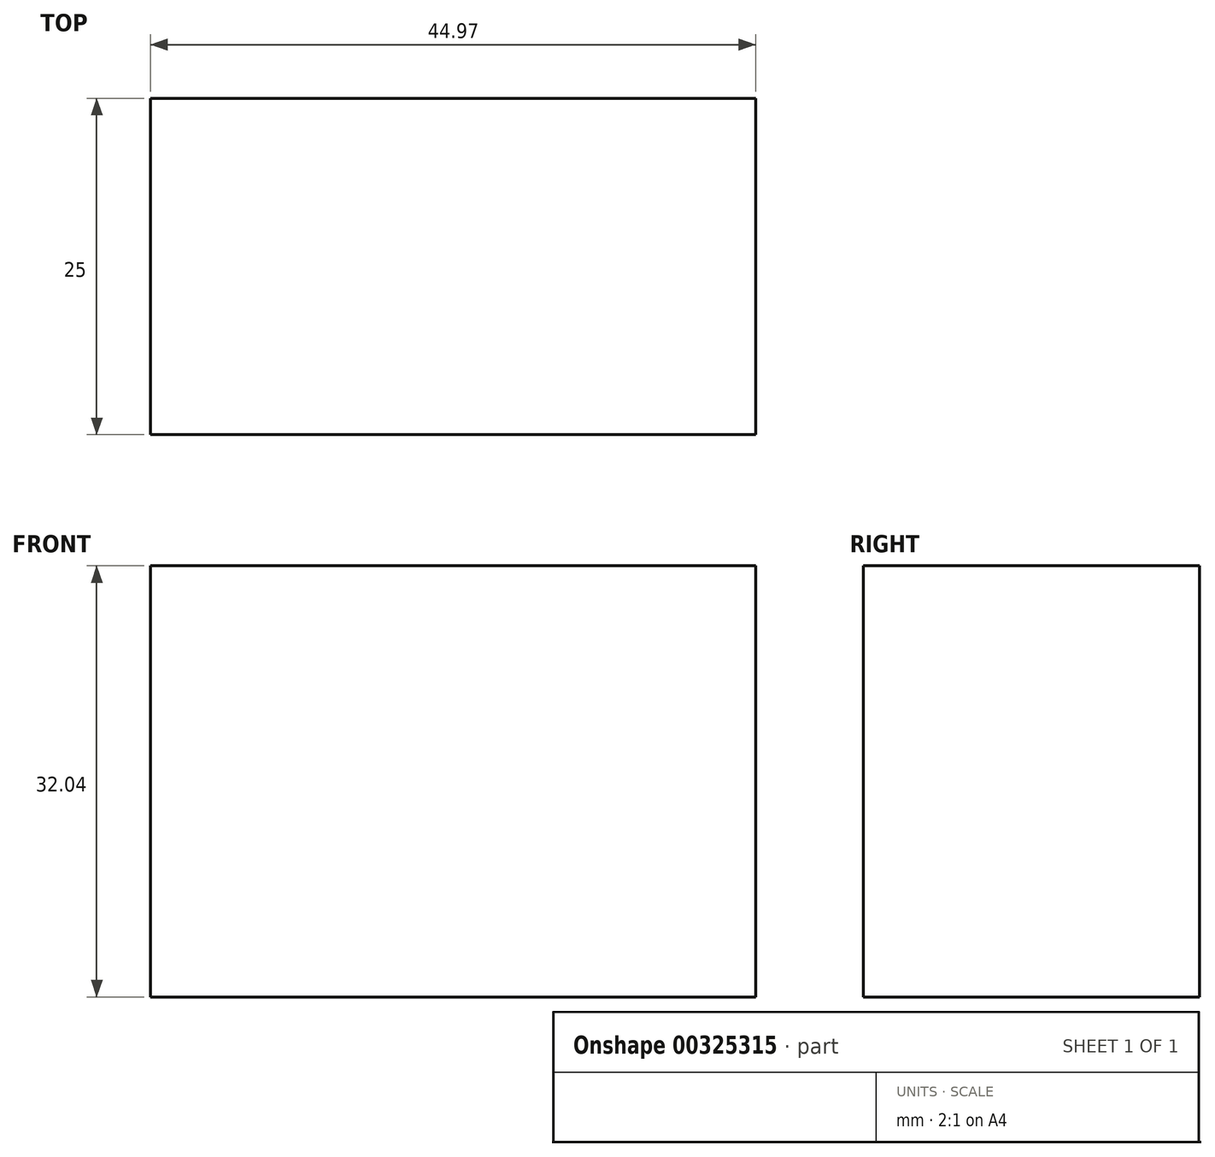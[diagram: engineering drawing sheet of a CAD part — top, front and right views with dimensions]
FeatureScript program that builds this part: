
annotation { "Feature Type Name" : "Feature", "Feature Type Description" : "" }
export const myFeature = defineFeature(function(context is Context, id is Id, definition is map)
    precondition{}
    {
        {
            var Q0;
            Q0=qCreatedBy(makeId("Front.planeOp"),FACE);
            var sketch = newSketch(context, id + "F0", { "sketchPlane" : qUnion([Q0])});
            skLineSegment(sketch, "E0.bottom", {"start": v(-64.93, 7.03) * mm, "end": v(-19.96, 7.03) * mm});
            skLineSegment(sketch, "E0.top", {"start": v(-64.93, 39.07) * mm, "end": v(-19.96, 39.07) * mm});
            skLineSegment(sketch, "E0.left", {"start": v(-64.93, 7.03) * mm, "end": v(-64.93, 39.07) * mm});
            skLineSegment(sketch, "E0.right", {"start": v(-19.96, 7.03) * mm, "end": v(-19.96, 39.07) * mm});
            skPoint(sketch, "E0.middle", {"position": v(-42.44, 23.05) * mm});
            skSolve(sketch);
        }
        {
            var Q0;
            Q0=makeQuery(id+"F0.imprint","IMPRINT",FACE,{"disambiguationData":[TD([[makeQuery(id+"F0.imprint","IMPRINT",EDGE,{"derivedFrom":sQuery(id+"F0.wireOp",EDGE,"E0.bottom")}),1.0]])]});
            extrude(context, id + "F1", {"entities" : qUnion([Q0]), "depth" : 25 * mm});
        }
    });
